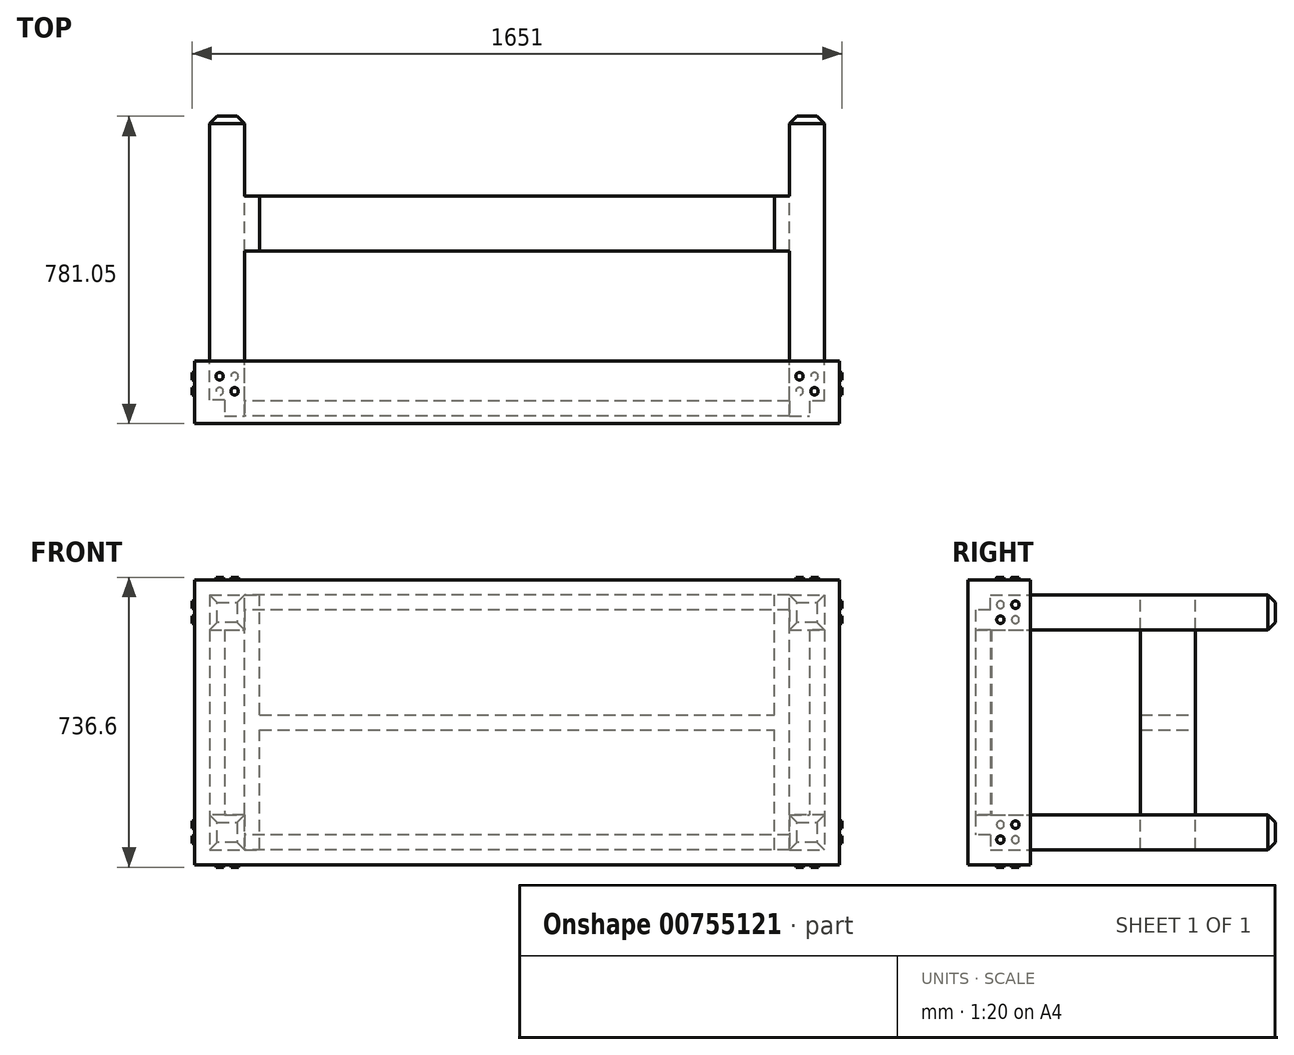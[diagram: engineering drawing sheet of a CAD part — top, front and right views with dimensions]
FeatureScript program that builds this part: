
annotation { "Feature Type Name" : "Feature", "Feature Type Description" : "" }
export const myFeature = defineFeature(function(context is Context, id is Id, definition is map)
    precondition{}
    {
        {
            var Q0;
            Q0=qCreatedBy(makeId("Front.planeOp"),FACE);
            var sketch = newSketch(context, id + "F0", { "sketchPlane" : qUnion([Q0])});
            skLineSegment(sketch, "E0.bottom", {"start": v(819.15, 361.95) * mm, "end": v(-819.15, 361.95) * mm});
            skLineSegment(sketch, "E0.top", {"start": v(819.15, -361.95) * mm, "end": v(-819.15, -361.95) * mm});
            skLineSegment(sketch, "E0.left", {"start": v(819.15, 361.95) * mm, "end": v(819.15, -361.95) * mm});
            skLineSegment(sketch, "E0.right", {"start": v(-819.15, 361.95) * mm, "end": v(-819.15, -361.95) * mm});
            skPoint(sketch, "E0.middle", {"position": v(0, 0) * mm});
            skSolve(sketch);
        }
        {
            var Q0;
            Q0 = qSketchRegion(id + "F0", true);
            extrude(context, id + "F1", {"entities" : qUnion([Q0]), "depth" : 19.05 * mm, "offsetDistance" : 25.4 * mm});
        }
        {
            var Q0;
            Q0=makeQuery(id+"F1.opExtrude","CAP_FACE",FACE,{"disambiguationData":[OSD([sQuery(id+"F0.wireOp",EDGE,"E0.bottom"),sQuery(id+"F0.wireOp",EDGE,"E0.top"),sQuery(id+"F0.wireOp",EDGE,"E0.left"),sQuery(id+"F0.wireOp",EDGE,"E0.right")])],"isStart":true});
            var sketch = newSketch(context, id + "F2", { "sketchPlane" : qUnion([Q0])});
            skLineSegment(sketch, "E1.bottom", {"start": v(819.15, 361.95) * mm, "end": v(-819.15, 361.95) * mm});
            skLineSegment(sketch, "E1.top", {"start": v(819.15, -361.95) * mm, "end": v(-819.15, -361.95) * mm});
            skLineSegment(sketch, "E1.left", {"start": v(819.15, 361.95) * mm, "end": v(819.15, -361.95) * mm});
            skLineSegment(sketch, "E1.right", {"start": v(-819.15, 361.95) * mm, "end": v(-819.15, -361.95) * mm});
            skPoint(sketch, "E1.middle", {"position": v(0, 0) * mm});
            skSolve(sketch);
        }
        {
            var Q0;
            Q0 = qSketchRegion(id + "F2", true);
            extrude(context, id + "F3", {"entities" : qUnion([Q0]), "operationType" : NewBodyOperationType.ADD, "depth" : 139.7 * mm, "offsetDistance" : 25.4 * mm});
        }
        {
            var Q0;
            Q0=makeQuery(id+"F3.opExtrude","CAP_FACE",FACE,{"disambiguationData":[OSD([sQuery(id+"F2.wireOp",EDGE,"E1.bottom"),sQuery(id+"F2.wireOp",EDGE,"E1.top"),sQuery(id+"F2.wireOp",EDGE,"E1.left"),sQuery(id+"F2.wireOp",EDGE,"E1.right")])],"isStart":false});
            var sketch = newSketch(context, id + "F4", { "sketchPlane" : qUnion([Q0])});
            skLineSegment(sketch, "E2.bottom", {"start": v(-692.15, 323.85) * mm, "end": v(-781.05, 323.85) * mm});
            skLineSegment(sketch, "E2.top", {"start": v(-692.15, 234.95) * mm, "end": v(-781.05, 234.95) * mm});
            skLineSegment(sketch, "E2.left", {"start": v(-692.15, 323.85) * mm, "end": v(-692.15, 234.95) * mm});
            skLineSegment(sketch, "E2.right", {"start": v(-781.05, 323.85) * mm, "end": v(-781.05, 234.95) * mm});
            skPoint(sketch, "E2.middle", {"position": v(-736.6, 279.4) * mm});
            skLineSegment(sketch, "E3.bottom", {"start": v(781.05, 323.85) * mm, "end": v(692.15, 323.85) * mm});
            skLineSegment(sketch, "E3.top", {"start": v(781.05, 234.95) * mm, "end": v(692.15, 234.95) * mm});
            skLineSegment(sketch, "E3.left", {"start": v(781.05, 323.85) * mm, "end": v(781.05, 234.95) * mm});
            skLineSegment(sketch, "E3.right", {"start": v(692.15, 323.85) * mm, "end": v(692.15, 234.95) * mm});
            skPoint(sketch, "E3.middle", {"position": v(736.6, 279.4) * mm});
            skLineSegment(sketch, "E4.bottom", {"start": v(781.05, -234.95) * mm, "end": v(692.15, -234.95) * mm});
            skLineSegment(sketch, "E4.top", {"start": v(781.05, -323.85) * mm, "end": v(692.15, -323.85) * mm});
            skLineSegment(sketch, "E4.left", {"start": v(781.05, -234.95) * mm, "end": v(781.05, -323.85) * mm});
            skLineSegment(sketch, "E4.right", {"start": v(692.15, -234.95) * mm, "end": v(692.15, -323.85) * mm});
            skPoint(sketch, "E4.middle", {"position": v(736.6, -279.4) * mm});
            skLineSegment(sketch, "E5.bottom", {"start": v(-692.15, -234.95) * mm, "end": v(-781.05, -234.95) * mm});
            skLineSegment(sketch, "E5.top", {"start": v(-692.15, -323.85) * mm, "end": v(-781.05, -323.85) * mm});
            skLineSegment(sketch, "E5.left", {"start": v(-692.15, -234.95) * mm, "end": v(-692.15, -323.85) * mm});
            skLineSegment(sketch, "E5.right", {"start": v(-781.05, -234.95) * mm, "end": v(-781.05, -323.85) * mm});
            skPoint(sketch, "E5.middle", {"position": v(-736.6, -279.4) * mm});
            skSolve(sketch);
        }
        {
            var Q0;
            Q0=makeQuery(id+"F4.imprint","IMPRINT",FACE,{"disambiguationData":[TD([[makeQuery(id+"F4.imprint","IMPRINT",EDGE,{"derivedFrom":sQuery(id+"F4.wireOp",EDGE,"E2.bottom")}),-1.0]])]});
            var sketch = newSketch(context, id + "F5", { "sketchPlane" : qUnion([Q0])});
            skLineSegment(sketch, "E6.bottom", {"start": v(-781.05, 323.85) * mm, "end": v(781.05, 323.85) * mm});
            skLineSegment(sketch, "E6.top", {"start": v(-781.05, -323.85) * mm, "end": v(781.05, -323.85) * mm});
            skLineSegment(sketch, "E6.left", {"start": v(-781.05, 323.85) * mm, "end": v(-781.05, -323.85) * mm});
            skLineSegment(sketch, "E6.right", {"start": v(781.05, 323.85) * mm, "end": v(781.05, -323.85) * mm});
            skPoint(sketch, "E6.middle", {"position": v(0, 0) * mm});
            skSolve(sketch);
        }
        {
            var Q0;
            Q0 = qSketchRegion(id + "F5", true);
            extrude(context, id + "F6", {"entities" : qUnion([Q0]), "operationType" : NewBodyOperationType.REMOVE, "oppositeDirection" : true, "depth" : 139.7 * mm, "offsetDistance" : 25.4 * mm});
        }
        {
            var Q0;
            Q0 = qSketchRegion(id + "F4", true);
            extrude(context, id + "F7", {"entities" : qUnion([Q0]), "operationType" : NewBodyOperationType.ADD, "oppositeDirection" : true, "depth" : 139.7 * mm, "offsetDistance" : 25.4 * mm, "hasSecondDirection" : true, "secondDirectionOppositeDirection" : false, "secondDirectionDepth" : 622.3 * mm});
        }
        {
            var Q0;
            Q0=makeQuery(id+"F7.opExtrude","SWEPT_FACE",FACE,{"disambiguationData":[OSD([sQuery(id+"F4.wireOp",EDGE,"E3.bottom")])]});
            var sketch = newSketch(context, id + "F8", { "sketchPlane" : qUnion([Q0])});
            skLineSegment(sketch, "E7.bottom", {"start": v(-692.15, 558.8) * mm, "end": v(-654.05, 558.8) * mm});
            skLineSegment(sketch, "E7.top", {"start": v(-692.15, 419.1) * mm, "end": v(-654.05, 419.1) * mm});
            skLineSegment(sketch, "E7.left", {"start": v(-692.15, 558.8) * mm, "end": v(-692.15, 419.1) * mm});
            skLineSegment(sketch, "E7.right", {"start": v(-654.05, 558.8) * mm, "end": v(-654.05, 419.1) * mm});
            skPoint(sketch, "E7.middle", {"position": v(-673.1, 488.95) * mm});
            skSolve(sketch);
        }
        {
            var Q0;
            Q0 = qSketchRegion(id + "F8", true);
            var Q1;
            Q1=makeQuery(id+"F1.opExtrude","SWEPT_BODY",BODY,{"disambiguationData":[OSD([sQuery(id+"F0.wireOp",EDGE,"E0.bottom"),sQuery(id+"F0.wireOp",EDGE,"E0.top"),sQuery(id+"F0.wireOp",EDGE,"E0.left"),sQuery(id+"F0.wireOp",EDGE,"E0.right")])]});
            extrude(context, id + "F9", {"entities" : qUnion([Q0]), "operationType" : NewBodyOperationType.ADD, "oppositeDirection" : true, "depth" : 647.7 * mm, "endBoundEntityBody" : qUnion([Q1]), "offsetDistance" : 25.4 * mm});
        }
        {
            var Q0;
            Q0=makeQuery(id+"F7.opExtrude","SWEPT_FACE",FACE,{"disambiguationData":[OSD([sQuery(id+"F4.wireOp",EDGE,"E2.bottom")])]});
            var sketch = newSketch(context, id + "F10", { "sketchPlane" : qUnion([Q0])});
            skLineSegment(sketch, "E8.bottom", {"start": v(692.15, 558.8) * mm, "end": v(654.05, 558.8) * mm});
            skLineSegment(sketch, "E8.top", {"start": v(692.15, 419.1) * mm, "end": v(654.05, 419.1) * mm});
            skLineSegment(sketch, "E8.left", {"start": v(692.15, 558.8) * mm, "end": v(692.15, 419.1) * mm});
            skLineSegment(sketch, "E8.right", {"start": v(654.05, 558.8) * mm, "end": v(654.05, 419.1) * mm});
            skPoint(sketch, "E8.middle", {"position": v(673.1, 488.95) * mm});
            skSolve(sketch);
        }
        {
            var Q0;
            Q0 = qSketchRegion(id + "F10", true);
            extrude(context, id + "F11", {"entities" : qUnion([Q0]), "operationType" : NewBodyOperationType.ADD, "oppositeDirection" : true, "depth" : 647.7 * mm, "offsetDistance" : 25.4 * mm});
        }
        {
            var Q0;
            Q0=makeQuery(id+"F7.opExtrude","CAP_EDGE",EDGE,{"disambiguationData":[OSD([sQuery(id+"F4.wireOp",EDGE,"E5.top")])],"isStart":true});
            var Q1;
            Q1=makeQuery(id+"F7.opExtrude","CAP_EDGE",EDGE,{"disambiguationData":[OSD([sQuery(id+"F4.wireOp",EDGE,"E5.right")])],"isStart":true});
            var Q2;
            Q2=makeQuery(id+"F7.opExtrude","CAP_EDGE",EDGE,{"disambiguationData":[OSD([sQuery(id+"F4.wireOp",EDGE,"E5.bottom")])],"isStart":true});
            var Q3;
            Q3=makeQuery(id+"F7.opExtrude","CAP_EDGE",EDGE,{"disambiguationData":[OSD([sQuery(id+"F4.wireOp",EDGE,"E5.left")])],"isStart":true});
            var Q4;
            Q4=makeQuery(id+"F7.opExtrude","CAP_EDGE",EDGE,{"disambiguationData":[OSD([sQuery(id+"F4.wireOp",EDGE,"E2.bottom")])],"isStart":true});
            var Q5;
            Q5=makeQuery(id+"F7.opExtrude","CAP_EDGE",EDGE,{"disambiguationData":[OSD([sQuery(id+"F4.wireOp",EDGE,"E2.left")])],"isStart":true});
            var Q6;
            Q6=makeQuery(id+"F7.opExtrude","CAP_EDGE",EDGE,{"disambiguationData":[OSD([sQuery(id+"F4.wireOp",EDGE,"E2.right")])],"isStart":true});
            var Q7;
            Q7=makeQuery(id+"F7.opExtrude","CAP_EDGE",EDGE,{"disambiguationData":[OSD([sQuery(id+"F4.wireOp",EDGE,"E2.top")])],"isStart":true});
            var Q8;
            Q8=makeQuery(id+"F7.opExtrude","CAP_EDGE",EDGE,{"disambiguationData":[OSD([sQuery(id+"F4.wireOp",EDGE,"E3.bottom")])],"isStart":true});
            var Q9;
            Q9=makeQuery(id+"F7.opExtrude","CAP_EDGE",EDGE,{"disambiguationData":[OSD([sQuery(id+"F4.wireOp",EDGE,"E3.top")])],"isStart":true});
            var Q10;
            Q10=makeQuery(id+"F7.opExtrude","CAP_EDGE",EDGE,{"disambiguationData":[OSD([sQuery(id+"F4.wireOp",EDGE,"E3.right")])],"isStart":true});
            var Q11;
            Q11=makeQuery(id+"F7.opExtrude","CAP_EDGE",EDGE,{"disambiguationData":[OSD([sQuery(id+"F4.wireOp",EDGE,"E3.left")])],"isStart":true});
            var Q12;
            Q12=makeQuery(id+"F7.opExtrude","CAP_EDGE",EDGE,{"disambiguationData":[OSD([sQuery(id+"F4.wireOp",EDGE,"E4.bottom")])],"isStart":true});
            var Q13;
            Q13=makeQuery(id+"F7.opExtrude","CAP_EDGE",EDGE,{"disambiguationData":[OSD([sQuery(id+"F4.wireOp",EDGE,"E4.left")])],"isStart":true});
            var Q14;
            Q14=makeQuery(id+"F7.opExtrude","CAP_EDGE",EDGE,{"disambiguationData":[OSD([sQuery(id+"F4.wireOp",EDGE,"E4.top")])],"isStart":true});
            var Q15;
            Q15=makeQuery(id+"F7.opExtrude","CAP_EDGE",EDGE,{"disambiguationData":[OSD([sQuery(id+"F4.wireOp",EDGE,"E4.right")])],"isStart":true});
            chamfer(context, id + "F12", {"entities" : qUnion([Q0, Q1, Q2, Q3, Q4, Q5, Q6, Q7, Q8, Q9, Q10, Q11, Q12, Q13, Q14, Q15]), "width" : 19.05 * mm, "tangentPropagation" : true});
        }
        {
            var Q0;
            Q0=makeQuery(id+"F3.boolean.opBoolean","MERGE",FACE,{"derivedFrom":[makeQuery(id+"F1.opExtrude","SWEPT_FACE",FACE,{"disambiguationData":[OSD([sQuery(id+"F0.wireOp",EDGE,"E0.bottom")])]}),makeQuery(id+"F3.opExtrude","SWEPT_FACE",FACE,{"disambiguationData":[OSD([sQuery(id+"F2.wireOp",EDGE,"E1.bottom")])]})]});
            var sketch = newSketch(context, id + "F13", { "sketchPlane" : qUnion([Q0])});
            skCircle(sketch, "E9", {"center": v(-755.65, 101.6) * mm, "radius": 9.53 * mm});
            skCircle(sketch, "E10", {"center": v(-717.55, 63.5) * mm, "radius": 9.53 * mm});
            skSolve(sketch);
        }
        {
            var Q0;
            Q0 = qSketchRegion(id + "F13", true);
            extrude(context, id + "F14", {"entities" : qUnion([Q0]), "operationType" : NewBodyOperationType.ADD, "depth" : 6.35 * mm, "offsetDistance" : 25.4 * mm, "hasSecondDirection" : true, "secondDirectionOppositeDirection" : true, "secondDirectionDepth" : 76.2 * mm});
        }
        {
            var Q0;
            Q0=makeQuery(id+"F11.opExtrude","SWEPT_FACE",FACE,{"disambiguationData":[OSD([sQuery(id+"F10.wireOp",EDGE,"E8.right")])]});
            var sketch = newSketch(context, id + "F15", { "sketchPlane" : qUnion([Q0])});
            skLineSegment(sketch, "E11.bottom", {"start": v(-419.1, 19.05) * mm, "end": v(-558.8, 19.05) * mm});
            skLineSegment(sketch, "E11.top", {"start": v(-419.1, -19.05) * mm, "end": v(-558.8, -19.05) * mm});
            skLineSegment(sketch, "E11.left", {"start": v(-419.1, 19.05) * mm, "end": v(-419.1, -19.05) * mm});
            skLineSegment(sketch, "E11.right", {"start": v(-558.8, 19.05) * mm, "end": v(-558.8, -19.05) * mm});
            skPoint(sketch, "E11.middle", {"position": v(-488.95, 0) * mm});
            skSolve(sketch);
        }
        {
            var Q0;
            Q0 = qSketchRegion(id + "F15", true);
            extrude(context, id + "F16", {"entities" : qUnion([Q0]), "operationType" : NewBodyOperationType.ADD, "depth" : 1308.1 * mm, "offsetDistance" : 25.4 * mm});
        }
        {
            var Q0;
            {var subQ0=sQuery(id+"F5.wireOp",EDGE,"E6.top");Q0=makeQuery(id+"F9.boolean.opBoolean","SPLIT",FACE,{"disambiguationData":[TD([makeQuery(id+"F6.boolean.opBoolean","COPY",FACE,{"derivedFrom":makeQuery(id+"F6.opExtrude","SWEPT_FACE",FACE,{"disambiguationData":[OSD([subQ0])]})})])],"derivedFrom":makeQuery(id+"F7.opExtrude","SWEPT_FACE",FACE,{"disambiguationData":[OSD([sQuery(id+"F4.wireOp",EDGE,"E4.right")])]})});}
            var sketch = newSketch(context, id + "F17", { "sketchPlane" : qUnion([Q0])});
            skLineSegment(sketch, "E12.bottom", {"start": v(38.1, -285.75) * mm, "end": v(0, -285.75) * mm});
            skLineSegment(sketch, "E12.top", {"start": v(38.1, -323.85) * mm, "end": v(0, -323.85) * mm});
            skLineSegment(sketch, "E12.left", {"start": v(38.1, -285.75) * mm, "end": v(38.1, -323.85) * mm});
            skLineSegment(sketch, "E12.right", {"start": v(0, -285.75) * mm, "end": v(0, -323.85) * mm});
            skPoint(sketch, "E12.middle", {"position": v(19.05, -304.8) * mm});
            skSolve(sketch);
        }
        {
            var Q0;
            Q0 = qSketchRegion(id + "F17", true);
            extrude(context, id + "F18", {"entities" : qUnion([Q0]), "operationType" : NewBodyOperationType.ADD, "depth" : 1384.3 * mm, "offsetDistance" : 25.4 * mm});
        }
        {
            var Q0;
            Q0=makeQuery(id+"F7.opExtrude","SWEPT_FACE",FACE,{"disambiguationData":[OSD([sQuery(id+"F4.wireOp",EDGE,"E5.bottom")])]});
            var sketch = newSketch(context, id + "F19", { "sketchPlane" : qUnion([Q0])});
            skLineSegment(sketch, "E13.bottom", {"start": v(781.05, 38.1) * mm, "end": v(742.95, 38.1) * mm});
            skLineSegment(sketch, "E13.top", {"start": v(781.05, 0) * mm, "end": v(742.95, 0) * mm});
            skLineSegment(sketch, "E13.left", {"start": v(781.05, 38.1) * mm, "end": v(781.05, 0) * mm});
            skLineSegment(sketch, "E13.right", {"start": v(742.95, 38.1) * mm, "end": v(742.95, 0) * mm});
            skPoint(sketch, "E13.middle", {"position": v(762, 19.05) * mm});
            skSolve(sketch);
        }
        {
            var Q0;
            Q0 = qSketchRegion(id + "F19", true);
            extrude(context, id + "F20", {"entities" : qUnion([Q0]), "operationType" : NewBodyOperationType.ADD, "depth" : 469.9 * mm, "offsetDistance" : 25.4 * mm});
        }
        {
            var Q0;
            Q0=makeQuery(id+"F7.opExtrude","SWEPT_FACE",FACE,{"disambiguationData":[OSD([sQuery(id+"F4.wireOp",EDGE,"E4.bottom")])]});
            var sketch = newSketch(context, id + "F21", { "sketchPlane" : qUnion([Q0])});
            skLineSegment(sketch, "E14.bottom", {"start": v(-742.95, 40.64) * mm, "end": v(-781.05, 40.64) * mm});
            skLineSegment(sketch, "E14.top", {"start": v(-742.95, 0) * mm, "end": v(-781.05, 0) * mm});
            skLineSegment(sketch, "E14.left", {"start": v(-742.95, 40.64) * mm, "end": v(-742.95, 0) * mm});
            skLineSegment(sketch, "E14.right", {"start": v(-781.05, 40.64) * mm, "end": v(-781.05, 0) * mm});
            skPoint(sketch, "E14.middle", {"position": v(-762, 20.32) * mm});
            skSolve(sketch);
        }
        {
            var Q0;
            Q0 = qSketchRegion(id + "F21", true);
            extrude(context, id + "F22", {"entities" : qUnion([Q0]), "operationType" : NewBodyOperationType.ADD, "depth" : 520.7 * mm, "offsetDistance" : 25.4 * mm});
        }
        {
            var Q0;
            {var subQ2=sQuery(id+"F5.wireOp",EDGE,"E6.bottom");Q0=makeQuery(id+"F9.boolean.opBoolean","SPLIT",FACE,{"disambiguationData":[TD([makeQuery(id+"F6.boolean.opBoolean","COPY",FACE,{"derivedFrom":makeQuery(id+"F6.opExtrude","SWEPT_FACE",FACE,{"disambiguationData":[OSD([subQ2])]})})])],"derivedFrom":makeQuery(id+"F7.opExtrude","SWEPT_FACE",FACE,{"disambiguationData":[OSD([sQuery(id+"F4.wireOp",EDGE,"E3.right")])]})});}
            var sketch = newSketch(context, id + "F23", { "sketchPlane" : qUnion([Q0])});
            skLineSegment(sketch, "E15.bottom", {"start": v(38.1, 285.75) * mm, "end": v(0, 285.75) * mm});
            skLineSegment(sketch, "E15.top", {"start": v(38.1, 323.85) * mm, "end": v(0, 323.85) * mm});
            skLineSegment(sketch, "E15.left", {"start": v(38.1, 285.75) * mm, "end": v(38.1, 323.85) * mm});
            skLineSegment(sketch, "E15.right", {"start": v(0, 285.75) * mm, "end": v(0, 323.85) * mm});
            skPoint(sketch, "E15.middle", {"position": v(19.05, 304.8) * mm});
            skSolve(sketch);
        }
        {
            var Q0;
            Q0 = qSketchRegion(id + "F23", true);
            extrude(context, id + "F24", {"entities" : qUnion([Q0]), "operationType" : NewBodyOperationType.ADD, "depth" : 1384.3 * mm, "offsetDistance" : 25.4 * mm});
        }
        {
            var Q0;
            Q0=makeQuery(id+"F3.boolean.opBoolean","MERGE",FACE,{"derivedFrom":[makeQuery(id+"F1.opExtrude","SWEPT_FACE",FACE,{"disambiguationData":[OSD([sQuery(id+"F0.wireOp",EDGE,"E0.bottom")])]}),makeQuery(id+"F3.opExtrude","SWEPT_FACE",FACE,{"disambiguationData":[OSD([sQuery(id+"F2.wireOp",EDGE,"E1.bottom")])]})]});
            var sketch = newSketch(context, id + "F25", { "sketchPlane" : qUnion([Q0])});
            skCircle(sketch, "E16", {"center": v(717.55, 101.6) * mm, "radius": 9.53 * mm});
            skCircle(sketch, "E17", {"center": v(755.65, 63.5) * mm, "radius": 9.53 * mm});
            skSolve(sketch);
        }
        {
            var Q0;
            Q0 = qSketchRegion(id + "F25", true);
            extrude(context, id + "F26", {"entities" : qUnion([Q0]), "operationType" : NewBodyOperationType.ADD, "depth" : 6.35 * mm, "offsetDistance" : 25.4 * mm, "hasSecondDirection" : true, "secondDirectionOppositeDirection" : true, "secondDirectionDepth" : 76.2 * mm});
        }
        {
            var Q0;
            Q0=makeQuery(id+"F3.boolean.opBoolean","MERGE",FACE,{"derivedFrom":[makeQuery(id+"F1.opExtrude","SWEPT_FACE",FACE,{"disambiguationData":[OSD([sQuery(id+"F0.wireOp",EDGE,"E0.right")])]}),makeQuery(id+"F3.opExtrude","SWEPT_FACE",FACE,{"disambiguationData":[OSD([sQuery(id+"F2.wireOp",EDGE,"E1.left")])]})]});
            var sketch = newSketch(context, id + "F27", { "sketchPlane" : qUnion([Q0])});
            skCircle(sketch, "E18", {"center": v(-101.6, 260.35) * mm, "radius": 9.53 * mm});
            skCircle(sketch, "E19", {"center": v(-63.5, 298.45) * mm, "radius": 9.53 * mm});
            skCircle(sketch, "E20", {"center": v(-101.6, -298.45) * mm, "radius": 9.53 * mm});
            skCircle(sketch, "E21", {"center": v(-63.5, -260.35) * mm, "radius": 9.53 * mm});
            skSolve(sketch);
        }
        {
            var Q0;
            Q0 = qSketchRegion(id + "F27", true);
            extrude(context, id + "F28", {"entities" : qUnion([Q0]), "operationType" : NewBodyOperationType.ADD, "depth" : 6.35 * mm, "offsetDistance" : 25.4 * mm, "hasSecondDirection" : true, "secondDirectionOppositeDirection" : true, "secondDirectionDepth" : 76.2 * mm});
        }
        {
            var Q0;
            Q0=makeQuery(id+"F3.boolean.opBoolean","MERGE",FACE,{"derivedFrom":[makeQuery(id+"F1.opExtrude","SWEPT_FACE",FACE,{"disambiguationData":[OSD([sQuery(id+"F0.wireOp",EDGE,"E0.left")])]}),makeQuery(id+"F3.opExtrude","SWEPT_FACE",FACE,{"disambiguationData":[OSD([sQuery(id+"F2.wireOp",EDGE,"E1.right")])]})]});
            var sketch = newSketch(context, id + "F29", { "sketchPlane" : qUnion([Q0])});
            skCircle(sketch, "E22", {"center": v(101.6, 298.45) * mm, "radius": 9.53 * mm});
            skCircle(sketch, "E23", {"center": v(101.6, -260.35) * mm, "radius": 9.53 * mm});
            skCircle(sketch, "E24", {"center": v(63.5, 260.35) * mm, "radius": 9.53 * mm});
            skCircle(sketch, "E25", {"center": v(63.5, -298.45) * mm, "radius": 9.53 * mm});
            skSolve(sketch);
        }
        {
            var Q0;
            Q0 = qSketchRegion(id + "F29", true);
            extrude(context, id + "F30", {"entities" : qUnion([Q0]), "operationType" : NewBodyOperationType.ADD, "depth" : 6.35 * mm, "offsetDistance" : 25.4 * mm, "hasSecondDirection" : true, "secondDirectionOppositeDirection" : true, "secondDirectionDepth" : 76.2 * mm});
        }
        {
            var Q0;
            Q0=makeQuery(id+"F3.boolean.opBoolean","MERGE",FACE,{"derivedFrom":[makeQuery(id+"F1.opExtrude","SWEPT_FACE",FACE,{"disambiguationData":[OSD([sQuery(id+"F0.wireOp",EDGE,"E0.top")])]}),makeQuery(id+"F3.opExtrude","SWEPT_FACE",FACE,{"disambiguationData":[OSD([sQuery(id+"F2.wireOp",EDGE,"E1.top")])]})]});
            var sketch = newSketch(context, id + "F31", { "sketchPlane" : qUnion([Q0])});
            skCircle(sketch, "E26", {"center": v(-755.65, -63.5) * mm, "radius": 9.53 * mm});
            skCircle(sketch, "E27", {"center": v(-717.55, -101.6) * mm, "radius": 9.53 * mm});
            skCircle(sketch, "E28", {"center": v(717.55, -63.5) * mm, "radius": 9.53 * mm});
            skCircle(sketch, "E29", {"center": v(755.65, -101.6) * mm, "radius": 9.53 * mm});
            skSolve(sketch);
        }
        {
            var Q0;
            Q0 = qSketchRegion(id + "F31", true);
            extrude(context, id + "F32", {"entities" : qUnion([Q0]), "operationType" : NewBodyOperationType.ADD, "depth" : 6.35 * mm, "offsetDistance" : 25.4 * mm, "hasSecondDirection" : true, "secondDirectionOppositeDirection" : true, "secondDirectionDepth" : 76.2 * mm});
        }
    });
